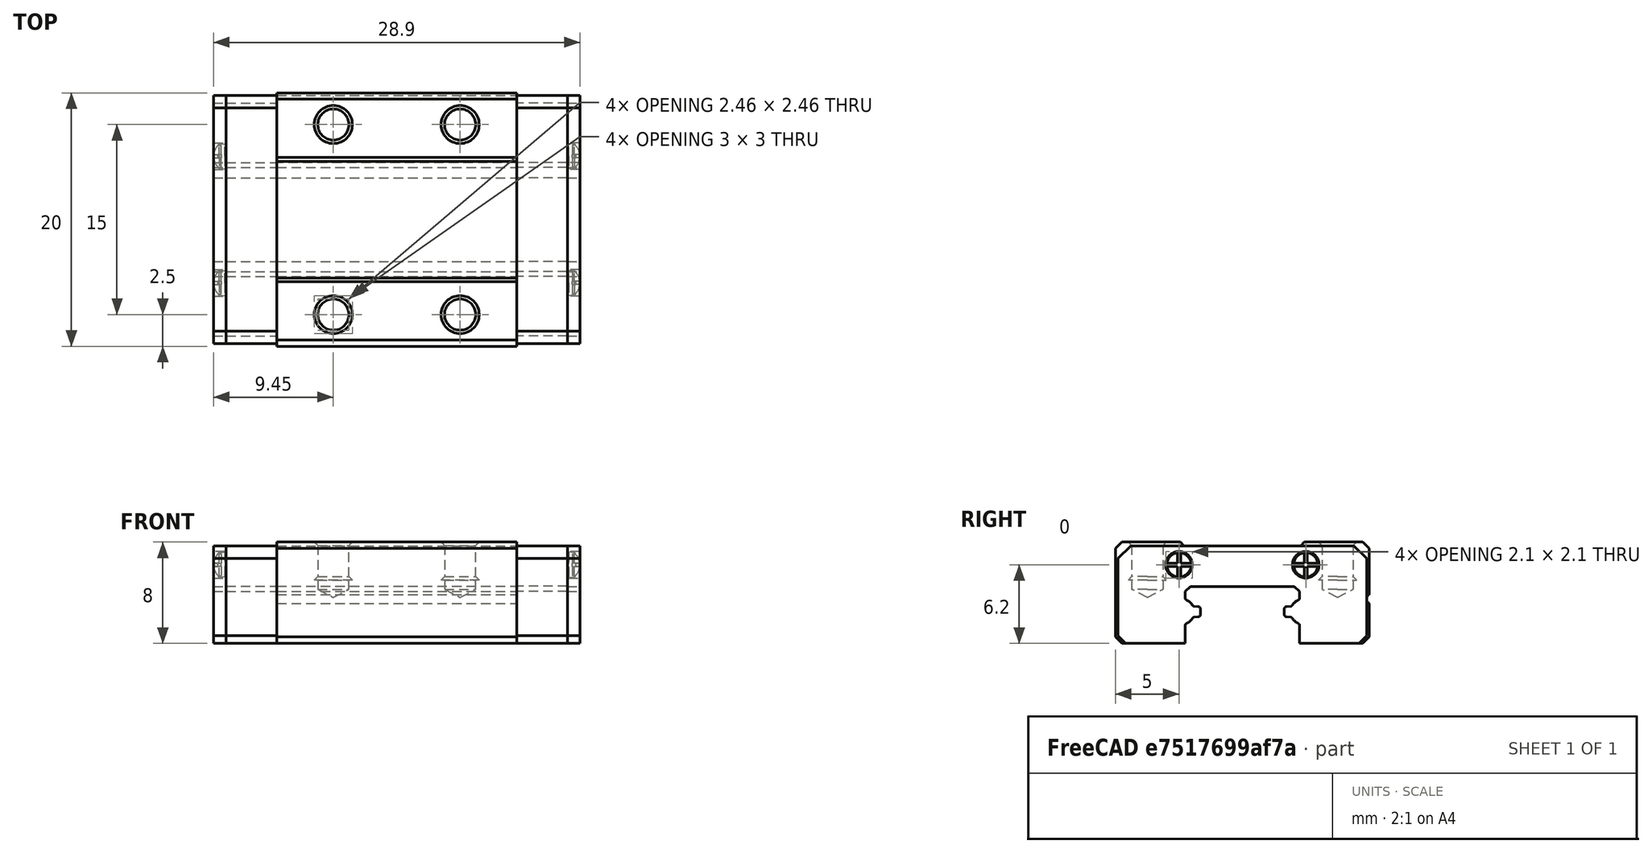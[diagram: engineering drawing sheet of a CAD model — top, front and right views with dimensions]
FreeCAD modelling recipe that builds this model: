
FCSTD DOCUMENT  (FreeCAD 2022.430R26244 +4758 (Git))
Label: as3MGN9CZFC-HiwinCorporation-3D-10-31-2021
License: All rights reserved
LicenseURL: http://en.wikipedia.org/wiki/All_rights_reserved
objects: Part::Feature×9, Part::FeaturePython×7, App::FeaturePython×2, App::LinkGroup×1
note: 15 computed .brp shape members not serialized (recipe doc carries the construction recipe); baked Part::Feature solids carry a one-line shape summary decoded from their .brp

FEATURE [App::FeaturePython] Constraints  # WARN: FeaturePython — macro-defined, semantics opaque (R4)
  TreeRank = 0
  _LinkVersion = 1
  _Version = 1
FEATURE [Part::Feature] Solid  label="PRODUCT_NAME_1"
  TreeRank = 11
  shape: bbox 18.9 x 20 x 8 mm, 90 faces (baked)
FEATURE [Part::Feature] Solid001  label="PRODUCT_NAME_2"
  TreeRank = 12
  shape: bbox 4 x 19.6 x 7.7 mm, 40 faces (baked)
FEATURE [Part::Feature] Solid002  label="PRODUCT_NAME_3"
  TreeRank = 13
  shape: bbox 4 x 19.6 x 7.7 mm, 40 faces (baked)
FEATURE [Part::Feature] Solid003  label="PRODUCT_NAME_4"
  TreeRank = 14
  shape: bbox 1 x 19.6 x 7.7 mm, 46 faces (baked)
FEATURE [Part::Feature] Solid004  label="PRODUCT_NAME_5"
  TreeRank = 15
  shape: bbox 1 x 19.6 x 7.7 mm, 46 faces (baked)
FEATURE [Part::Feature] Solid005  label="PRODUCT_NAME_6"
  TreeRank = 16
  shape: bbox 0.9 x 2 x 2 mm, 18 faces (baked)
FEATURE [Part::Feature] Solid006  label="PRODUCT_NAME_7"
  TreeRank = 17
  shape: bbox 0.9 x 2 x 2 mm, 18 faces (baked)
FEATURE [Part::Feature] Solid007  label="PRODUCT_NAME_8"
  TreeRank = 18
  shape: bbox 0.9 x 2 x 2 mm, 18 faces (baked)
FEATURE [Part::Feature] Solid008  label="PRODUCT_NAME_9"
  TreeRank = 19
  shape: bbox 0.9 x 2 x 2 mm, 18 faces (baked)
FEATURE [App::LinkGroup] LinkGroup
  ElementList = -> [Solid,Solid001,Solid002,Solid003,Solid004,Solid005,Solid006,Solid007,Solid008]
  LinkMode = 0
  TreeRank = 20
  _LinkVersion = 1
FEATURE [Part::FeaturePython] Parts  # WARN: FeaturePython — macro-defined, semantics opaque (R4)
  Group = -> [LinkGroup]
  GroupMode = 0
  TreeRank = 0
  _LinkVersion = 1
FEATURE [Part::FeaturePython] Assembly  label="As3MGN9CZFC-HiwinCorporation-3D-10-31-2021"  # WARN: FeaturePython — macro-defined, semantics opaque (R4)
  AutoRelax = true
  BuildShape = 0
  Freeze = true
  Group = -> [Constraints,Elements,Parts]
  TreeRank = 0
  Verbose = false
  _LinkVersion = 1
  _SolverType = 1
  _Version = 1
FEATURE [App::FeaturePython] Elements  # WARN: FeaturePython — macro-defined, semantics opaque (R4)
  Group = -> [Element,Element001,Element002,Element003,Element004]
  TreeRank = 0
  _LinkVersion = 1
FEATURE [Part::FeaturePython] Element  label="Ref"  # link proxy (typed FeaturePython)
  Detach = false
  LinkTransform = true
  LinkedObject = -> LinkGroup [Solid.Face79]
  TreeRank = 21
  _LinkVersion = 1
  _Parent = -> Elements
FEATURE [Part::FeaturePython] Element001  label="Fix1"  # link proxy (typed FeaturePython)
  Detach = false
  LinkTransform = true
  LinkedObject = -> LinkGroup [Solid.Edge201]
  TreeRank = 22
  _LinkVersion = 1
  _Parent = -> Elements
FEATURE [Part::FeaturePython] Element002  label="Fix2"  # link proxy (typed FeaturePython)
  Detach = false
  LinkTransform = true
  LinkedObject = -> LinkGroup [Solid.Edge57]
  TreeRank = 23
  _LinkVersion = 1
  _Parent = -> Elements
FEATURE [Part::FeaturePython] Element003  label="Lat"  # link proxy (typed FeaturePython)
  Detach = false
  LinkTransform = true
  LinkedObject = -> LinkGroup [Solid.Face37]
  TreeRank = 24
  _LinkVersion = 1
  _Parent = -> Elements
FEATURE [Part::FeaturePython] Element004  # link proxy (typed FeaturePython)
  Detach = false
  LinkTransform = true
  LinkedObject = -> LinkGroup [Solid004.Face43]
  TreeRank = 25
  _LinkVersion = 1
  _Parent = -> Elements
